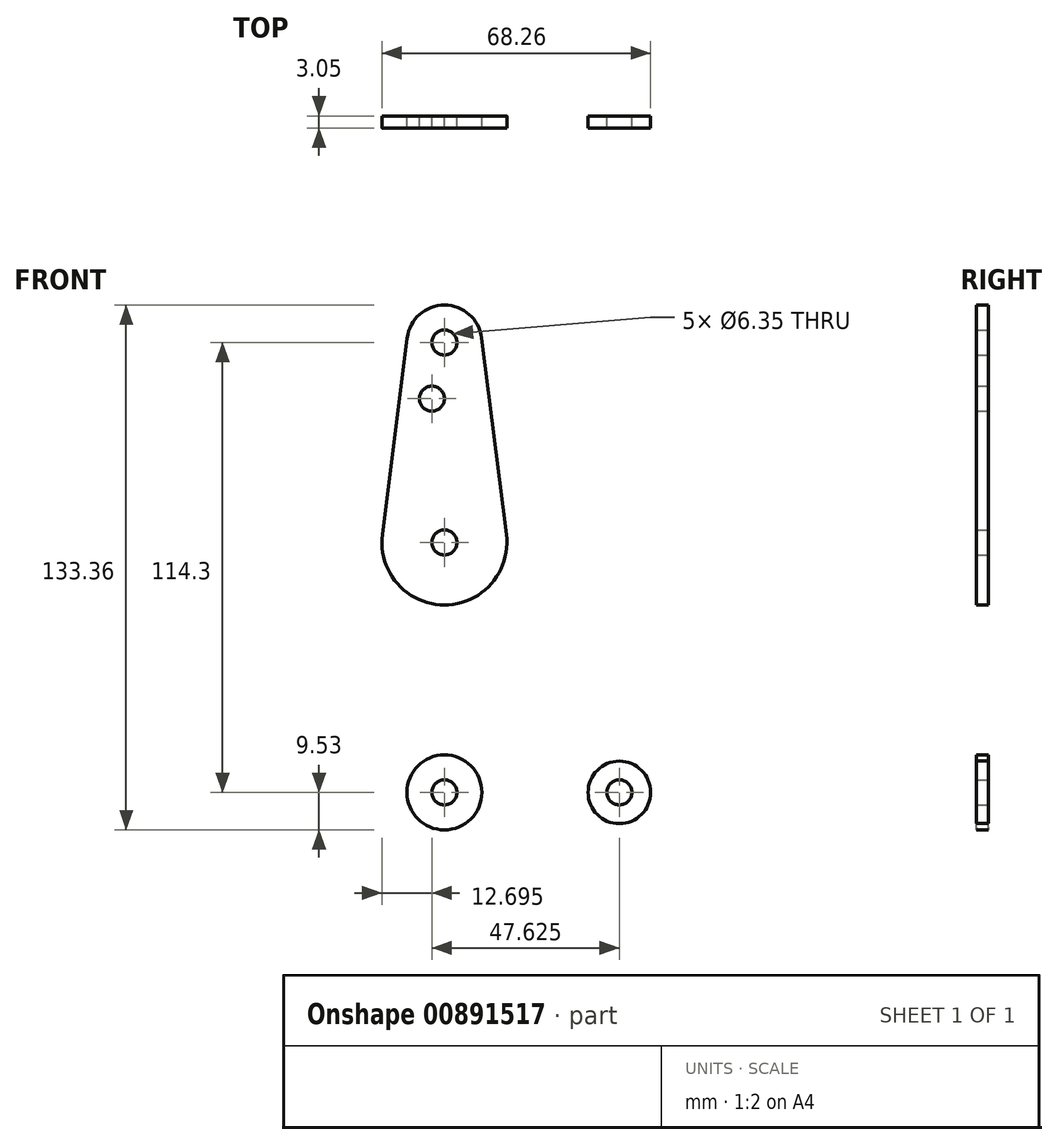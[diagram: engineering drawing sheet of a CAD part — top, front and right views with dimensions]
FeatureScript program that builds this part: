
annotation { "Feature Type Name" : "Feature", "Feature Type Description" : "" }
export const myFeature = defineFeature(function(context is Context, id is Id, definition is map)
    precondition{}
    {
        {
            var Q0;
            Q0=qCreatedBy(makeId("Front.planeOp"),FACE);
            var sketch = newSketch(context, id + "F0", { "sketchPlane" : qUnion([Q0])});
            skLineSegment(sketch, "E0", {"start": v(0, 114.3) * mm, "end": v(0, 0) * mm, "construction": true});
            skLineSegment(sketch, "E1", {"start": v(0, 0) * mm, "end": v(44.45, 0) * mm, "construction": true});
            skCircle(sketch, "E2", {"center": v(0, 114.3) * mm, "radius": 9.53 * mm});
            skCircle(sketch, "E3", {"center": v(0, 63.5) * mm, "radius": 15.88 * mm});
            skCircle(sketch, "E4", {"center": v(0, 0) * mm, "radius": 9.53 * mm});
            skCircle(sketch, "E5", {"center": v(44.45, 0) * mm, "radius": 7.94 * mm});
            skLineSegment(sketch, "E6", {"start": v(-9.45, 115.5) * mm, "end": v(-15.75, 65.48) * mm});
            skLineSegment(sketch, "E7", {"start": v(9.45, 115.5) * mm, "end": v(15.75, 65.48) * mm});
            skLineSegment(sketch, "E8", {"start": v(-15.8, 61.91) * mm, "end": v(-9.57, 0) * mm});
            skLineSegment(sketch, "E9", {"start": v(15.8, 61.91) * mm, "end": v(11.34, 17.59) * mm});
            skLineSegment(sketch, "E10", {"start": v(44.73, 7.93) * mm, "end": v(18.97, 8.85) * mm});
            skLineSegment(sketch, "E11", {"start": v(44.73, -7.93) * mm, "end": v(0.34, -9.52) * mm});
            skPoint(sketch, "E12.newPointB", {"position": v(0.34, 9.51) * mm});
            skArc(sketch, "E12.filletArc", {"start": v(11.34, 17.59) * mm, "mid": v(13.26, 11.57) * mm, "end": v(18.97, 8.85) * mm});
            skCircle(sketch, "E13", {"center": v(-3.18, 100.03) * mm, "radius": 3.18 * mm});
            skCircle(sketch, "E14", {"center": v(0, 114.3) * mm, "radius": 3.18 * mm});
            skCircle(sketch, "E15", {"center": v(0, 63.5) * mm, "radius": 3.18 * mm});
            skCircle(sketch, "E16", {"center": v(0, 0) * mm, "radius": 3.18 * mm});
            skCircle(sketch, "E17", {"center": v(44.45, 0) * mm, "radius": 3.18 * mm});
            skSolve(sketch);
        }
        {
            var Q0;
            Q0 = qSketchRegion(id + "F0", true);
            extrude(context, id + "F1", {"entities" : qUnion([Q0]), "depth" : 3.05 * mm, "offsetDistance" : 25.4 * mm});
        }
    });
